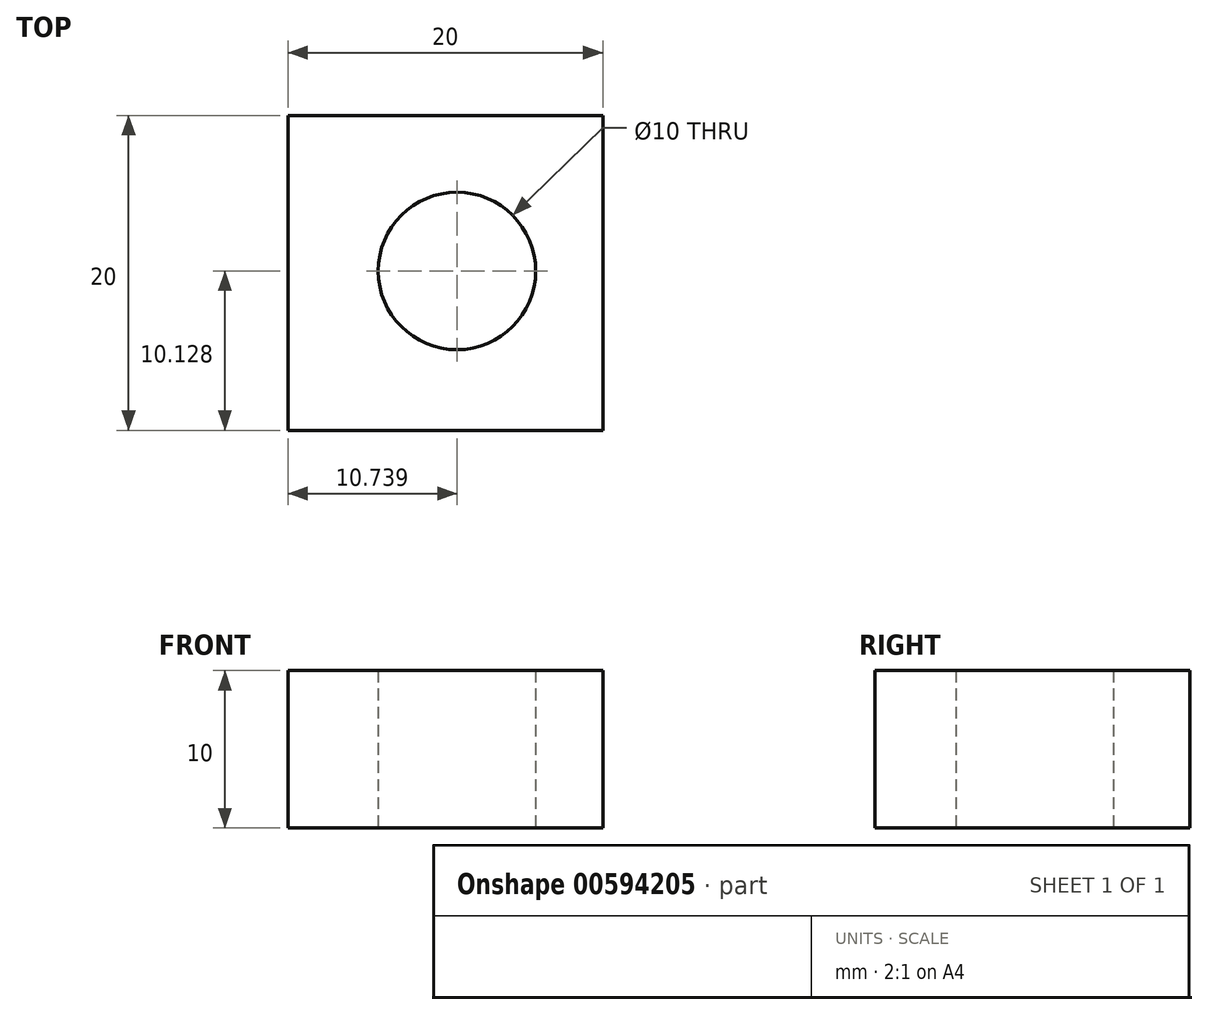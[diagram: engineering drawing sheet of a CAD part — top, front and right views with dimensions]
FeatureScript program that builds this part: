
annotation { "Feature Type Name" : "Feature", "Feature Type Description" : "" }
export const myFeature = defineFeature(function(context is Context, id is Id, definition is map)
    precondition{}
    {
        {
            var Q0;
            Q0=qCreatedBy(makeId("Top.planeOp"),FACE);
            var sketch = newSketch(context, id + "F0", { "sketchPlane" : qUnion([Q0])});
            skLineSegment(sketch, "E0.bottom", {"start": v(-14.69, 22.2) * mm, "end": v(5.31, 22.2) * mm});
            skLineSegment(sketch, "E0.top", {"start": v(-14.69, 2.2) * mm, "end": v(5.31, 2.2) * mm});
            skLineSegment(sketch, "E0.left", {"start": v(-14.69, 22.2) * mm, "end": v(-14.69, 2.2) * mm});
            skLineSegment(sketch, "E0.right", {"start": v(5.31, 22.2) * mm, "end": v(5.31, 2.2) * mm});
            skCircle(sketch, "E1", {"center": v(-3.95, 12.34) * mm, "radius": 5 * mm});
            skSolve(sketch);
        }
        {
            var Q0;
            Q0=makeQuery(id+"F0.imprint","IMPRINT",FACE,{"disambiguationData":[TD([[makeQuery(id+"F0.imprint","IMPRINT",EDGE,{"derivedFrom":sQuery(id+"F0.wireOp",EDGE,"E0.bottom")}),-1.0]])]});
            extrude(context, id + "F1", {"entities" : qUnion([Q0]), "depth" : 10 * mm, "offsetDistance" : 25 * mm});
        }
    });
